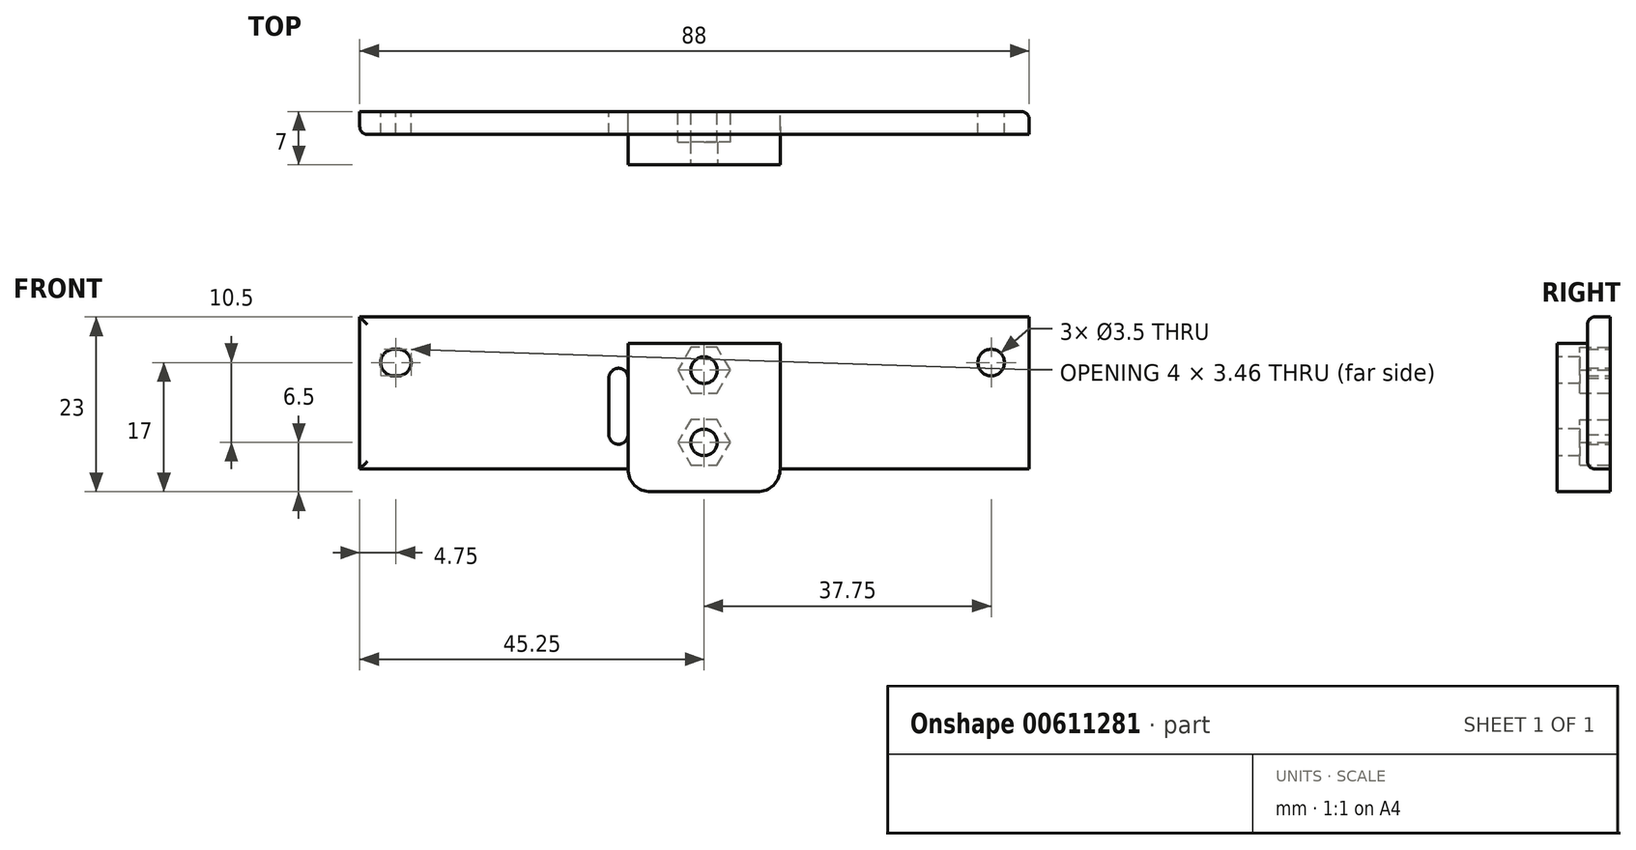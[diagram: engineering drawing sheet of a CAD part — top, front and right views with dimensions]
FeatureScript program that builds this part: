
annotation { "Feature Type Name" : "Feature", "Feature Type Description" : "" }
export const myFeature = defineFeature(function(context is Context, id is Id, definition is map)
    precondition{}
    {
        {
            var Q0;
            Q0=qCreatedBy(makeId("Front.planeOp"),FACE);
            var sketch = newSketch(context, id + "F0", { "sketchPlane" : qUnion([Q0])});
            skLineSegment(sketch, "E0.bottom", {"start": v(0, 0) * mm, "end": v(88, 0) * mm});
            skLineSegment(sketch, "E0.top", {"start": v(0, -20) * mm, "end": v(88, -20) * mm});
            skLineSegment(sketch, "E0.left", {"start": v(0, 0) * mm, "end": v(0, -20) * mm});
            skLineSegment(sketch, "E0.right", {"start": v(88, 0) * mm, "end": v(88, -20) * mm});
            skLineSegment(sketch, "E1", {"start": v(0, -6) * mm, "end": v(88, -6) * mm, "construction": true});
            skCircle(sketch, "E2", {"center": v(5, -6) * mm, "radius": 1.75 * mm});
            skCircle(sketch, "E3", {"center": v(83, -6) * mm, "radius": 1.75 * mm});
            skLineSegment(sketch, "E4", {"start": v(34, 0) * mm, "end": v(34, -20) * mm, "construction": true});
            skLineSegment(sketch, "E5", {"start": v(29, 0) * mm, "end": v(29, -20) * mm, "construction": true});
            skCircle(sketch, "E6", {"center": v(34, -15.5) * mm, "radius": 1.25 * mm});
            skCircle(sketch, "E7", {"center": v(34, -8) * mm, "radius": 1.25 * mm});
            skLineSegment(sketch, "E8", {"start": v(32.75, -7.96) * mm, "end": v(32.75, -15.54) * mm});
            skLineSegment(sketch, "E9", {"start": v(35.25, -8) * mm, "end": v(35.25, -15.5) * mm});
            skCircle(sketch, "E10", {"center": v(4.5, -6) * mm, "radius": 1.75 * mm});
            skSolve(sketch);
        }
        {
            var Q0;
            Q0=makeQuery(id+"F0.imprint","IMPRINT",FACE,{"disambiguationData":[TD([[makeQuery(id+"F0.imprint","IMPRINT",EDGE,{"derivedFrom":sQuery(id+"F0.wireOp",EDGE,"E0.bottom")}),-1.0]])]});
            var Q1;
            {var subQ0=sQuery(id+"F0.wireOp",EDGE,"15iexOeU-ugz1-MKlF-6M2T-YhLcArKAafTG");Q1=makeQuery(id+"F0.imprint","IMPRINT",FACE,{"disambiguationData":[TD([[makeQuery(id+"F0.imprint","IMPRINT",EDGE,{"derivedFrom":subQ0}),1.0]])]});}
            var Q2;
            {var subQ0=sQuery(id+"F0.wireOp",EDGE,"H0GDkFHR-dLBK-ekd7-CxMc-WgrPsWZYSiNL");var subQ1=makeQuery(id+"F0.imprint","INTERSECT",VERTEX,{"derivedFrom":[subQ0,sQuery(id+"F0.wireOp",EDGE,"15iexOeU-ugz1-MKlF-6M2T-YhLcArKAafTG")]});Q2=makeQuery(id+"F0.imprint","IMPRINT",FACE,{"disambiguationData":[TD([[makeQuery(id+"F0.imprint","IMPRINT",EDGE,{"disambiguationData":[TD([[subQ1,1.0]])],"derivedFrom":subQ0}),1.0]])]});}
            var Q3;
            {var subQ0=sQuery(id+"F0.wireOp",EDGE,"N8Qwdsn7-yQef-os47-0KRG-1ICMin2xKuaN");var subQ1=makeQuery(id+"F0.imprint","INTERSECT",VERTEX,{"derivedFrom":[subQ0,sQuery(id+"F0.wireOp",EDGE,"15iexOeU-ugz1-MKlF-6M2T-YhLcArKAafTG")]});Q3=makeQuery(id+"F0.imprint","IMPRINT",FACE,{"disambiguationData":[TD([[makeQuery(id+"F0.imprint","IMPRINT",EDGE,{"disambiguationData":[TD([[subQ1,1.0]])],"derivedFrom":subQ0}),1.0]])]});}
            extrude(context, id + "F1", {"entities" : qUnion([Q0, Q1, Q2, Q3]), "depth" : 3 * mm, "offsetDistance" : 25 * mm});
        }
        {
            var Q0;
            Q0=makeQuery(id+"F1.opExtrude","CAP_FACE",FACE,{"disambiguationData":[OSD([sQuery(id+"F0.wireOp",EDGE,"E0.bottom"),sQuery(id+"F0.wireOp",EDGE,"E0.top"),sQuery(id+"F0.wireOp",EDGE,"E0.left"),sQuery(id+"F0.wireOp",EDGE,"E0.right"),sQuery(id+"F0.wireOp",EDGE,"E2"),sQuery(id+"F0.wireOp",EDGE,"E3"),sQuery(id+"F0.wireOp",EDGE,"E6"),sQuery(id+"F0.wireOp",EDGE,"E7"),sQuery(id+"F0.wireOp",EDGE,"E8"),sQuery(id+"F0.wireOp",EDGE,"E9")])],"isStart":false});
            var sketch = newSketch(context, id + "F2", { "sketchPlane" : qUnion([Q0])});
            skLineSegment(sketch, "E11.bottom", {"start": v(35.25, -15.5) * mm, "end": v(55.25, -15.5) * mm});
            skLineSegment(sketch, "E11.top", {"start": v(35.25, -8) * mm, "end": v(55.25, -8) * mm});
            skLineSegment(sketch, "E11.left", {"start": v(35.25, -15.5) * mm, "end": v(35.25, -8) * mm});
            skLineSegment(sketch, "E11.right", {"start": v(55.25, -15.5) * mm, "end": v(55.25, -8) * mm});
            skLineSegment(sketch, "E12.top", {"start": v(35.25, -20) * mm, "end": v(55.25, -20) * mm});
            skLineSegment(sketch, "E12.left", {"start": v(35.25, -15.5) * mm, "end": v(35.25, -20) * mm});
            skLineSegment(sketch, "E12.right", {"start": v(55.25, -15.5) * mm, "end": v(55.25, -20) * mm});
            skLineSegment(sketch, "E13.top", {"start": v(35.25, -3.5) * mm, "end": v(55.25, -3.5) * mm});
            skLineSegment(sketch, "E13.left", {"start": v(35.25, -8) * mm, "end": v(35.25, -3.5) * mm});
            skLineSegment(sketch, "E13.right", {"start": v(55.25, -8) * mm, "end": v(55.25, -3.5) * mm});
            skSolve(sketch);
        }
        {
            var Q0;
            Q0=makeQuery(id+"F2.imprint","IMPRINT",FACE,{"disambiguationData":[TD([[makeQuery(id+"F2.imprint","IMPRINT",EDGE,{"derivedFrom":sQuery(id+"F2.wireOp",EDGE,"E11.top")}),1.0]])]});
            var Q1;
            Q1=makeQuery(id+"F2.imprint","IMPRINT",FACE,{"disambiguationData":[TD([[makeQuery(id+"F2.imprint","IMPRINT",EDGE,{"derivedFrom":sQuery(id+"F2.wireOp",EDGE,"E11.left")}),1.0]])]});
            var Q2;
            Q2=makeQuery(id+"F2.imprint","IMPRINT",FACE,{"disambiguationData":[TD([[makeQuery(id+"F2.imprint","IMPRINT",EDGE,{"derivedFrom":sQuery(id+"F2.wireOp",EDGE,"E11.bottom")}),-1.0]])]});
            extrude(context, id + "F3", {"entities" : qUnion([Q0, Q1, Q2]), "operationType" : NewBodyOperationType.ADD, "depth" : 4 * mm, "offsetDistance" : 25 * mm});
        }
        {
            var Q0;
            Q0=makeQuery(id+"F3.opExtrude","CAP_FACE",FACE,{"disambiguationData":[OSD([sQuery(id+"F2.wireOp",EDGE,"E11.left"),sQuery(id+"F2.wireOp",EDGE,"E11.right"),sQuery(id+"F2.wireOp",EDGE,"E12.top"),sQuery(id+"F2.wireOp",EDGE,"E12.left"),sQuery(id+"F2.wireOp",EDGE,"E12.right"),sQuery(id+"F2.wireOp",EDGE,"E13.top"),sQuery(id+"F2.wireOp",EDGE,"E13.left"),sQuery(id+"F2.wireOp",EDGE,"E13.right")])],"isStart":false});
            var sketch = newSketch(context, id + "F4", { "sketchPlane" : qUnion([Q0])});
            skLineSegment(sketch, "E14", {"start": v(35.25, -11.75) * mm, "end": v(55.25, -11.75) * mm, "construction": true});
            skLineSegment(sketch, "E15", {"start": v(35.25, -7) * mm, "end": v(55.25, -7) * mm, "construction": true});
            skLineSegment(sketch, "E16", {"start": v(35.25, -16.5) * mm, "end": v(55.25, -16.5) * mm, "construction": true});
            skCircle(sketch, "E17", {"center": v(45.25, -7) * mm, "radius": 1.75 * mm});
            skCircle(sketch, "E18", {"center": v(45.25, -16.5) * mm, "radius": 1.75 * mm});
            skSolve(sketch);
        }
        {
            var Q0;
            Q0=makeQuery(id+"F1.opExtrude","CAP_FACE",FACE,{"disambiguationData":[OSD([sQuery(id+"F0.wireOp",EDGE,"E0.bottom"),sQuery(id+"F0.wireOp",EDGE,"E0.top"),sQuery(id+"F0.wireOp",EDGE,"E0.left"),sQuery(id+"F0.wireOp",EDGE,"E0.right"),sQuery(id+"F0.wireOp",EDGE,"E2"),sQuery(id+"F0.wireOp",EDGE,"E3"),sQuery(id+"F0.wireOp",EDGE,"E6"),sQuery(id+"F0.wireOp",EDGE,"E7"),sQuery(id+"F0.wireOp",EDGE,"E8"),sQuery(id+"F0.wireOp",EDGE,"E9")])],"isStart":true});
            var sketch = newSketch(context, id + "F5", { "sketchPlane" : qUnion([Q0])});
            skLineSegment(sketch, "E19", {"start": v(-88, -16.5) * mm, "end": v(0, -16.5) * mm, "construction": true});
            skLineSegment(sketch, "E20", {"start": v(-88, -7) * mm, "end": v(0, -7) * mm, "construction": true});
            skCircle(sketch, "E21.cCircle", {"center": v(-45.25, -7) * mm, "radius": 3 * mm, "construction": true});
            skLineSegment(sketch, "E21.0", {"start": v(-46.98, -4) * mm, "end": v(-43.52, -4) * mm});
            skLineSegment(sketch, "E21.1", {"start": v(-43.52, -4) * mm, "end": v(-41.79, -7) * mm});
            skLineSegment(sketch, "E21.2", {"start": v(-41.79, -7) * mm, "end": v(-43.52, -10) * mm});
            skLineSegment(sketch, "E21.3", {"start": v(-43.52, -10) * mm, "end": v(-46.98, -10) * mm});
            skLineSegment(sketch, "E21.4", {"start": v(-46.98, -10) * mm, "end": v(-48.71, -7) * mm});
            skLineSegment(sketch, "E21.5", {"start": v(-48.71, -7) * mm, "end": v(-46.98, -4) * mm});
            skPoint(sketch, "E21.0.midPoint", {"position": v(-45.25, -4) * mm});
            skCircle(sketch, "E22.cCircle", {"center": v(-45.25, -16.5) * mm, "radius": 3 * mm, "construction": true});
            skLineSegment(sketch, "E22.0", {"start": v(-46.98, -13.5) * mm, "end": v(-43.52, -13.5) * mm});
            skLineSegment(sketch, "E22.1", {"start": v(-43.52, -13.5) * mm, "end": v(-41.79, -16.5) * mm});
            skLineSegment(sketch, "E22.2", {"start": v(-41.79, -16.5) * mm, "end": v(-43.52, -19.5) * mm});
            skLineSegment(sketch, "E22.3", {"start": v(-43.52, -19.5) * mm, "end": v(-46.98, -19.5) * mm});
            skLineSegment(sketch, "E22.4", {"start": v(-46.98, -19.5) * mm, "end": v(-48.71, -16.5) * mm});
            skLineSegment(sketch, "E22.5", {"start": v(-48.71, -16.5) * mm, "end": v(-46.98, -13.5) * mm});
            skPoint(sketch, "E22.0.midPoint", {"position": v(-45.25, -13.5) * mm});
            skSolve(sketch);
        }
        {
            var Q0;
            Q0=makeQuery(id+"F5.imprint","IMPRINT",FACE,{"disambiguationData":[TD([[makeQuery(id+"F5.imprint","IMPRINT",EDGE,{"derivedFrom":sQuery(id+"F5.wireOp",EDGE,"E21.0")}),-1.0]])]});
            var Q1;
            Q1=makeQuery(id+"F5.imprint","IMPRINT",FACE,{"disambiguationData":[TD([[makeQuery(id+"F5.imprint","IMPRINT",EDGE,{"derivedFrom":sQuery(id+"F5.wireOp",EDGE,"E22.0")}),-1.0]])]});
            extrude(context, id + "F6", {"entities" : qUnion([Q0, Q1]), "operationType" : NewBodyOperationType.REMOVE, "oppositeDirection" : true, "depth" : 4 * mm, "offsetDistance" : 25 * mm});
        }
        {
            var Q0;
            Q0=makeQuery(id+"F4.imprint","IMPRINT",FACE,{"disambiguationData":[TD([[makeQuery(id+"F4.imprint","IMPRINT",EDGE,{"derivedFrom":sQuery(id+"F4.wireOp",EDGE,"E17")}),1.0]])]});
            var Q1;
            Q1=makeQuery(id+"F4.imprint","IMPRINT",FACE,{"disambiguationData":[TD([[makeQuery(id+"F4.imprint","IMPRINT",EDGE,{"derivedFrom":sQuery(id+"F4.wireOp",EDGE,"E18")}),1.0]])]});
            extrude(context, id + "F7", {"entities" : qUnion([Q0, Q1]), "operationType" : NewBodyOperationType.REMOVE, "oppositeDirection" : true, "depth" : 25 * mm, "offsetDistance" : 25 * mm});
        }
        {
            var Q0;
            Q0=makeQuery(id+"F3.boolean.opBoolean","MERGE",FACE,{"derivedFrom":[makeQuery(id+"F1.opExtrude","SWEPT_FACE",FACE,{"disambiguationData":[OSD([sQuery(id+"F0.wireOp",EDGE,"E0.top")])]}),makeQuery(id+"F3.opExtrude","SWEPT_FACE",FACE,{"disambiguationData":[OSD([sQuery(id+"F2.wireOp",EDGE,"E12.top")])]})]});
            var sketch = newSketch(context, id + "F8", { "sketchPlane" : qUnion([Q0])});
            skLineSegment(sketch, "E23.bottom", {"start": v(55.25, 7) * mm, "end": v(35.25, 7) * mm});
            skLineSegment(sketch, "E23.top", {"start": v(55.25, 0) * mm, "end": v(35.25, 0) * mm});
            skLineSegment(sketch, "E23.left", {"start": v(55.25, 7) * mm, "end": v(55.25, 0) * mm});
            skLineSegment(sketch, "E23.right", {"start": v(35.25, 7) * mm, "end": v(35.25, 0) * mm});
            skSolve(sketch);
        }
        {
            var Q0;
            {var subQ12=sQuery(id+"F8.wireOp",EDGE,"E23.bottom");Q0=makeQuery(id+"F8.imprint","IMPRINT",FACE,{"disambiguationData":[TD([[makeQuery(id+"F8.imprint","IMPRINT",EDGE,{"derivedFrom":subQ12}),-1.0]])]});}
            extrude(context, id + "F9", {"entities" : qUnion([Q0]), "operationType" : NewBodyOperationType.ADD, "depth" : 3 * mm, "offsetDistance" : 25 * mm});
        }
        {
            var Q0;
            Q0=makeQuery(id+"F9.opExtrude","CAP_EDGE",EDGE,{"disambiguationData":[OSD([sQuery(id+"F8.wireOp",EDGE,"E23.right")])],"isStart":false});
            var Q1;
            Q1=makeQuery(id+"F9.opExtrude","CAP_EDGE",EDGE,{"disambiguationData":[OSD([sQuery(id+"F8.wireOp",EDGE,"E23.left")])],"isStart":false});
            fillet(context, id + "F10", {"entities" : qUnion([Q0, Q1]), "radius" : 3 * mm, "tangentPropagation" : true, "allowEdgeOverflow" : false});
        }
        {
            var Q0;
            Q0=makeQuery(id+"F1.opExtrude","CAP_EDGE",EDGE,{"disambiguationData":[OSD([sQuery(id+"F0.wireOp",EDGE,"E0.bottom")])],"isStart":false});
            var Q1;
            Q1=makeQuery(id+"F1.opExtrude","CAP_EDGE",EDGE,{"disambiguationData":[OSD([sQuery(id+"F0.wireOp",EDGE,"E0.right")])],"isStart":true});
            var Q2;
            {var subQ0=sQuery(id+"F0.wireOp",EDGE,"E0.right");var subQ1=sQuery(id+"F0.wireOp",EDGE,"E0.top");Q2=makeQuery(id+"F3.boolean.opBoolean","SPLIT",EDGE,{"disambiguationData":[TD([makeQuery(id+"F1.opExtrude","SWEPT_FACE",FACE,{"disambiguationData":[OSD([subQ0])]})])],"derivedFrom":makeQuery(id+"F1.opExtrude","CAP_EDGE",EDGE,{"disambiguationData":[OSD([subQ1])],"isStart":false})});}
            var Q3;
            {var subQ1=sQuery(id+"F0.wireOp",EDGE,"E0.left");var subQ2=sQuery(id+"F0.wireOp",EDGE,"E0.top");Q3=makeQuery(id+"F3.boolean.opBoolean","SPLIT",EDGE,{"disambiguationData":[TD([makeQuery(id+"F1.opExtrude","SWEPT_FACE",FACE,{"disambiguationData":[OSD([subQ1])]})])],"derivedFrom":makeQuery(id+"F1.opExtrude","CAP_EDGE",EDGE,{"disambiguationData":[OSD([subQ2])],"isStart":false})});}
            var Q4;
            Q4=makeQuery(id+"F1.opExtrude","CAP_EDGE",EDGE,{"disambiguationData":[OSD([sQuery(id+"F0.wireOp",EDGE,"E0.left")])],"isStart":false});
            fillet(context, id + "F11", {"entities" : qUnion([Q0, Q1, Q2, Q3, Q4]), "radius" : 1 * mm, "tangentPropagation" : true, "allowEdgeOverflow" : false});
        }
    });
